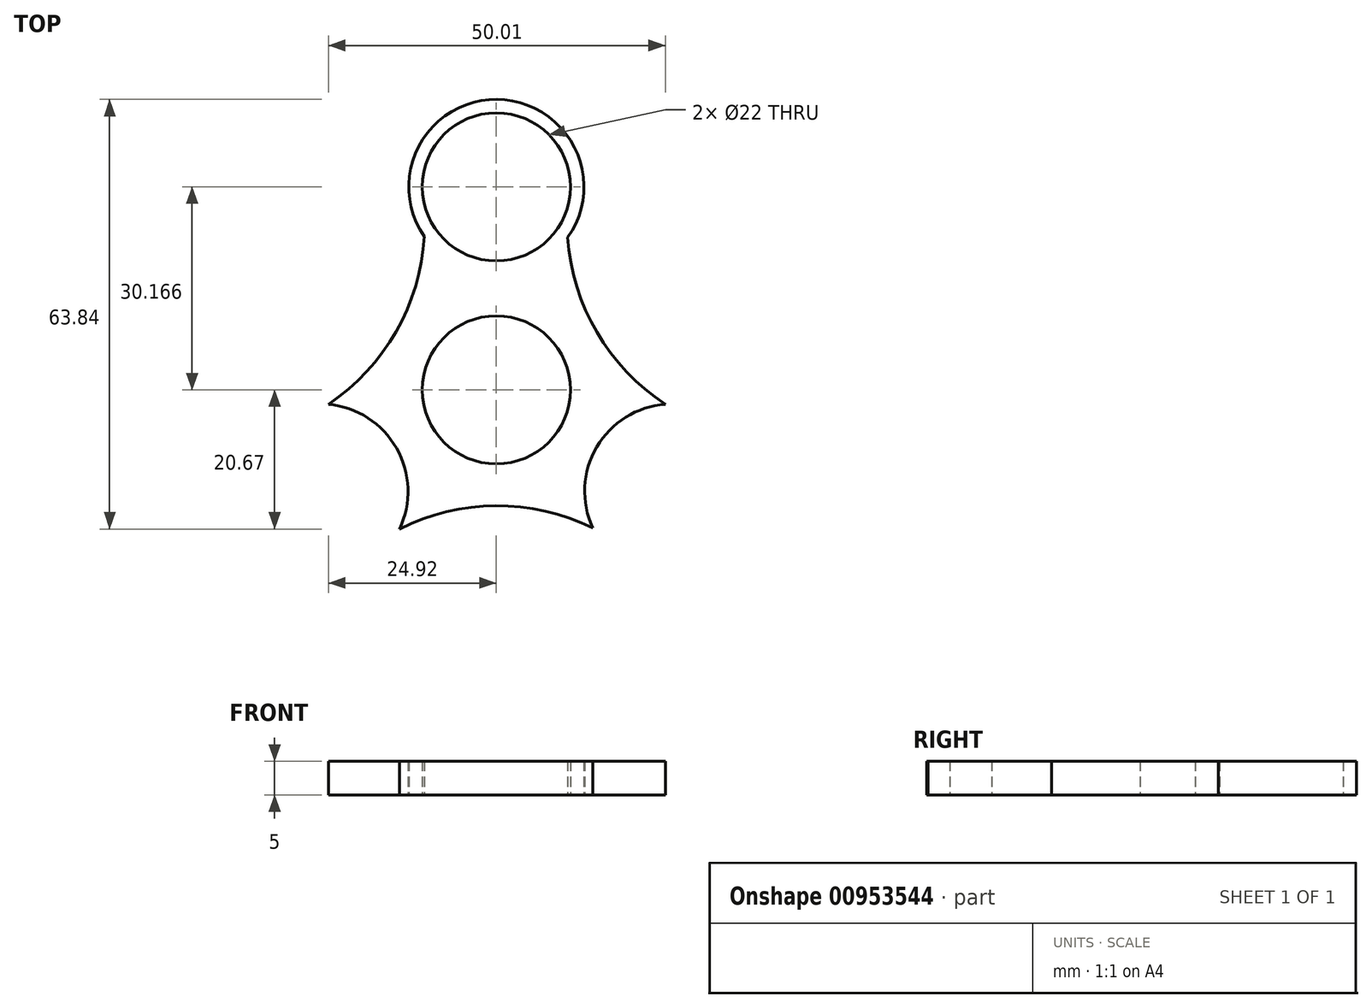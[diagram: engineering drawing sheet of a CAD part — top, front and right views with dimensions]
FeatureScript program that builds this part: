
annotation { "Feature Type Name" : "Feature", "Feature Type Description" : "" }
export const myFeature = defineFeature(function(context is Context, id is Id, definition is map)
    precondition{}
    {
        {
            var Q0;
            Q0=qCreatedBy(makeId("Top.planeOp"),FACE);
            var sketch = newSketch(context, id + "F0", { "sketchPlane" : qUnion([Q0])});
            skCircle(sketch, "E0", {"center": v(0, 0) * mm, "radius": 11 * mm});
            skCircle(sketch, "E1", {"center": v(0, 30.17) * mm, "radius": 11 * mm});
            skCircle(sketch, "E2.1.0", {"center": v(-26.12, -15.08) * mm, "radius": 11 * mm});
            skCircle(sketch, "E2.2.0", {"center": v(26.12, -15.08) * mm, "radius": 11 * mm});
            skCircle(sketch, "E3", {"center": v(0, 30.17) * mm, "radius": 13 * mm});
            skCircle(sketch, "E4.1.0", {"center": v(-26.12, -15.08) * mm, "radius": 13 * mm});
            skCircle(sketch, "E4.2.0", {"center": v(26.12, -15.08) * mm, "radius": 13 * mm});
            skArc(sketch, "E5", {"start": v(14.31, -20.5) * mm, "mid": v(-0.06, -17.22) * mm, "end": v(-14.39, -20.67) * mm});
            skArc(sketch, "E6.1.0", {"start": v(10.6, 22.65) * mm, "mid": v(14.94, 8.56) * mm, "end": v(25.1, -2.12) * mm});
            skArc(sketch, "E6.2.0", {"start": v(-24.92, -2.14) * mm, "mid": v(-14.88, 8.66) * mm, "end": v(-10.7, 22.8) * mm});
            skSolve(sketch);
        }
        {
            var Q0;
            Q0=makeQuery(id+"F0.imprint","IMPRINT",FACE,{"disambiguationData":[TD([[makeQuery(id+"F0.imprint","IMPRINT",EDGE,{"derivedFrom":sQuery(id+"F0.wireOp",EDGE,"E2.1.0")}),-1.0]])]});
            var Q1;
            Q1=makeQuery(id+"F0.imprint","IMPRINT",FACE,{"disambiguationData":[TD([[makeQuery(id+"F0.imprint","IMPRINT",EDGE,{"derivedFrom":sQuery(id+"F0.wireOp",EDGE,"E2.2.0")}),-1.0]])]});
            var Q2;
            Q2=makeQuery(id+"F0.imprint","IMPRINT",FACE,{"disambiguationData":[TD([[makeQuery(id+"F0.imprint","IMPRINT",EDGE,{"derivedFrom":sQuery(id+"F0.wireOp",EDGE,"E1")}),-1.0]])]});
            var Q3;
            Q3=makeQuery(id+"F0.imprint","IMPRINT",FACE,{"disambiguationData":[TD([[makeQuery(id+"F0.imprint","IMPRINT",EDGE,{"derivedFrom":sQuery(id+"F0.wireOp",EDGE,"E0")}),-1.0]])]});
            extrude(context, id + "F1", {"entities" : qUnion([Q0, Q1, Q2, Q3]), "depth" : 5 * mm, "offsetDistance" : 25 * mm});
        }
    });
